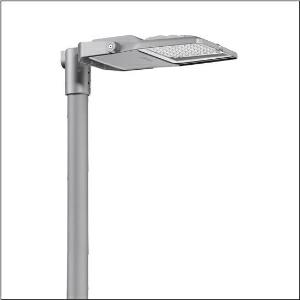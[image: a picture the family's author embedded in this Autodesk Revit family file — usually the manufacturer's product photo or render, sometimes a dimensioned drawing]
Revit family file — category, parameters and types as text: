
# Revit family: floodlight_fl_21_mini___pl64_5xa7775d2e3a_010e
name_source: partatom
category: Lighting Fixtures
units: mm (PartAtom-declared; Revit-internal decimal feet)

## family parameters
Cut with Voids When Loaded = No
Host = Face
Light Source = No
Part Type = Normal
Room Calculation Point = No
Round Connector Dimension = Use Diameter
Shared = No

## types (1)
- --- (1 x LED, 17220 lm, 142.9 W, 3000K)
    Apparent Load = 143 VA
    CIE Flux Codes = 28 80 98 100 100
    Color Rendering = 70
    Color Temperature = 3000K
    Default Elevation = 1800 mm
    Description = Floodlight FL 21 mini, floodlight, primary light control with lens, of PMMA, primary optical cover: protective disc, of toughened safety glass, transparent, light distribution: PL64, light emission: direct distribution, installation type: surface-mounted, LED, High Power LED, rated luminous flux: 17.220lm, luminous efficacy: 121lm/W, light colour: 730, colour temperature: 3000K, control: flexible luminous flux parameterisation, time-dependent luminous flux control, constant luminous flux control, overheat protection, pre-setting: logarithmic dimming characteristic, with terminal, 6-pole, mains connection: 220..240V, AC, 50/60Hz, start of lifetime: 143W, end of service life: 151W, reduction: 63W, luminaire housing, of diecast aluminium, powder-coated, Siteco® metallic grey (DB 702S), corrosivity category C5 mid according to DIN EN ISO 12944, sealing non-destructively replaceable, please order mast flange separately, mast bracket, of steel, galvanised, powder-coated, Siteco® metallic grey (DB 702S), Smart Interface above, protection rating (complete): IP66, insulation class (complete): insulation class II (safety insulation), certification: CE, ENEC, VDE, protection symbol: D, impact resistance: IK08, permissible operating ambient temperature: -40..+40°C, permissible operating ambient temperature for outdoor applications: -40..+50°C, standard: DIN EN 12944, LABS conformity tested according to VDMA 24364:2018-05, packaging unit: 1 piece

Light Distribution: PL64
    Height = 70 mm
    Lamp = 1 x LED
    Lamp Light Flux = 17220 lm
    Lamp Power = 142.9 W
    Lamp count = 1
    Length = 485 mm
    Luminous efficacy = 121 lm/W
    Manufacturer = Siteco
    ModVariant = No
    Model = 5XA7775D2E3A
    Number of Poles = 1
    OnlyDefault = Yes
    Power Factor = 1
    Product Name = Floodlight FL 21 mini | PL64
    Product group = floodlight | pylon annexe
    ProductGroupID = 6200
    Protection Class = Protection class II
    Protection Degree = IP 66
    RLX_Detail_Level = 1
    RLX_Emergency_Light_Flux = 0 lm
    RLX_Emergency_Type = 0
    RLX_Emergency_Type_DB = No
    RlxData = <blob elided: 101325 chars, md5=839d53f4>
    Socket = socket
    Standby Power = 0 W
    System Light Flux = 17220 lm
    System Power = 143 W
    Type Comments = factory setting: luminous flux: 100 % | dim-lin: 254 | 730 mA
    Type Image = l_1007125.jpg
    URL = http://relux.com
    VarID = @adj_135609
    Voltage = 0 V
    Weight = 0.00 kg
    Width = 337 mm

## geometry (parser evidence)
native form markers: Blend x4, Sweep x11
no freeform markers — native parametric forms only
